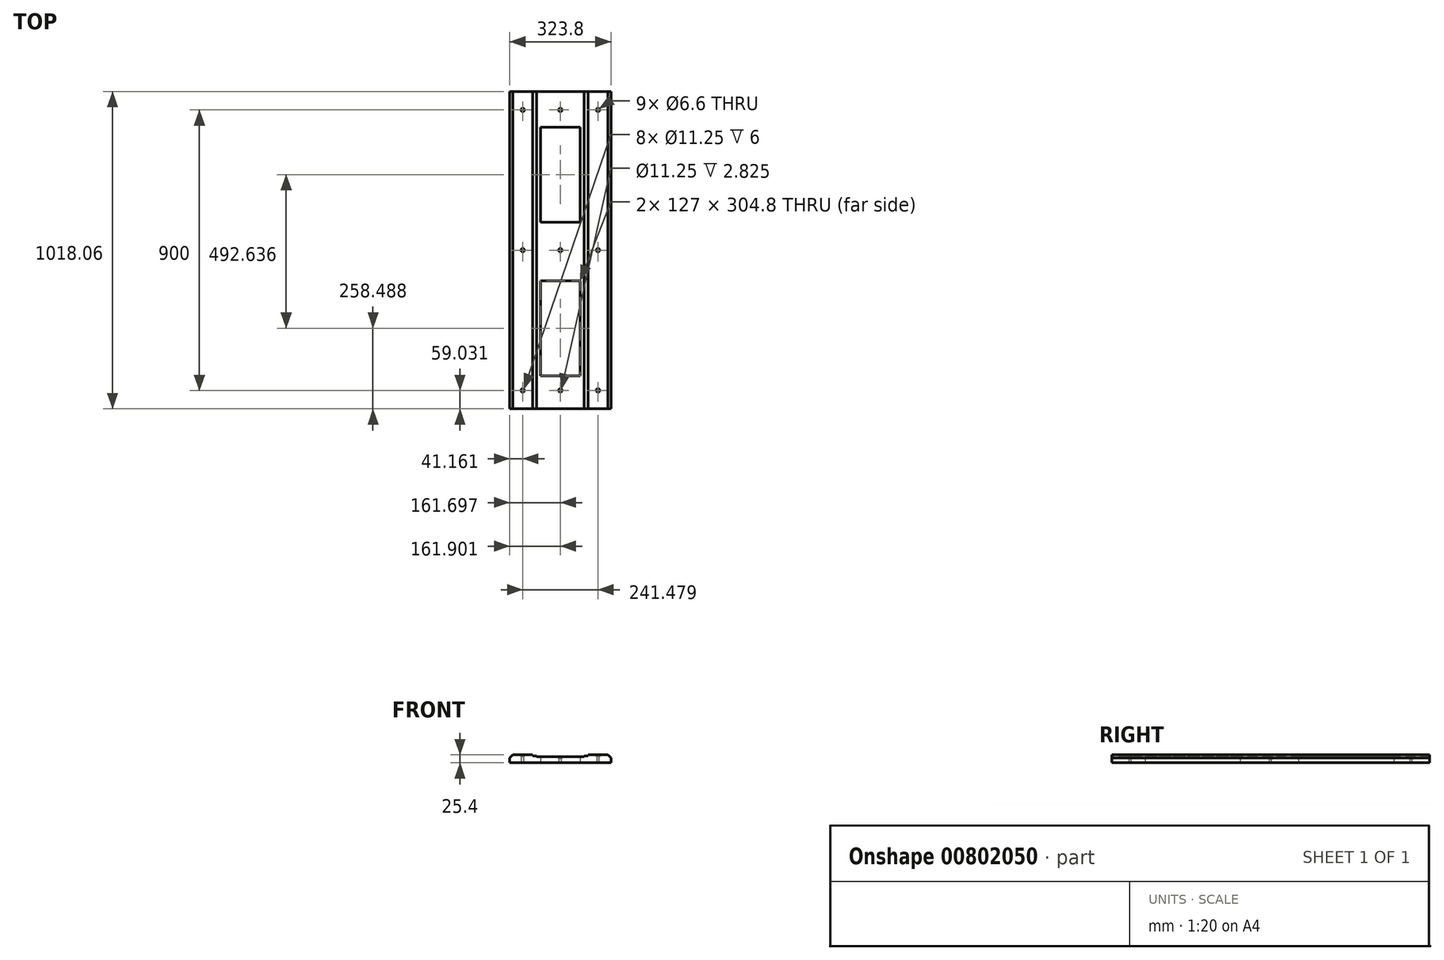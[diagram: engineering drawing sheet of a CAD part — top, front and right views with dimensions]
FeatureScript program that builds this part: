
annotation { "Feature Type Name" : "Feature", "Feature Type Description" : "" }
export const myFeature = defineFeature(function(context is Context, id is Id, definition is map)
    precondition{}
    {
        {
            var Q0;
            Q0=qCreatedBy(makeId("Top.planeOp"),FACE);
            var sketch = newSketch(context, id + "F0", { "sketchPlane" : qUnion([Q0])});
            skLineSegment(sketch, "E0.bottom", {"start": v(0, 0) * mm, "end": v(-323.8, 0) * mm});
            skLineSegment(sketch, "E0.top", {"start": v(0, 1018.06) * mm, "end": v(-323.8, 1018.06) * mm});
            skLineSegment(sketch, "E0.left", {"start": v(0, 0) * mm, "end": v(0, 1018.06) * mm});
            skLineSegment(sketch, "E0.right", {"start": v(-323.8, 0) * mm, "end": v(-323.8, 1018.06) * mm});
            skLineSegment(sketch, "E1.bottom", {"start": v(-225.6, 903.52) * mm, "end": v(-98.6, 903.52) * mm});
            skLineSegment(sketch, "E1.top", {"start": v(-225.6, 598.72) * mm, "end": v(-98.6, 598.72) * mm});
            skLineSegment(sketch, "E1.left", {"start": v(-225.6, 903.52) * mm, "end": v(-225.6, 598.72) * mm});
            skLineSegment(sketch, "E1.right", {"start": v(-98.6, 903.52) * mm, "end": v(-98.6, 598.72) * mm});
            skLineSegment(sketch, "E2.bottom", {"start": v(-225.6, 410.89) * mm, "end": v(-98.6, 410.89) * mm});
            skLineSegment(sketch, "E2.top", {"start": v(-225.6, 106.09) * mm, "end": v(-98.6, 106.09) * mm});
            skLineSegment(sketch, "E2.left", {"start": v(-225.6, 410.89) * mm, "end": v(-225.6, 106.09) * mm});
            skLineSegment(sketch, "E2.right", {"start": v(-98.6, 410.89) * mm, "end": v(-98.6, 106.09) * mm});
            skSolve(sketch);
        }
        {
            var Q0;
            Q0=qSketchRegion(id+"F0",true);
            extrude(context, id + "F1", {"entities" : qUnion([Q0]), "depth" : 25.4 * mm});
        }
        {
            var Q0;
            Q0=makeQuery(id+"F1.opExtrude","CAP_FACE",FACE,{"disambiguationData":[OSD([sQuery(id+"F0.wireOp",EDGE,"E0.bottom"),sQuery(id+"F0.wireOp",EDGE,"E0.top"),sQuery(id+"F0.wireOp",EDGE,"E0.left"),sQuery(id+"F0.wireOp",EDGE,"E0.right"),sQuery(id+"F0.wireOp",EDGE,"E1.bottom"),sQuery(id+"F0.wireOp",EDGE,"E1.top"),sQuery(id+"F0.wireOp",EDGE,"E1.left"),sQuery(id+"F0.wireOp",EDGE,"E1.right"),sQuery(id+"F0.wireOp",EDGE,"E2.bottom"),sQuery(id+"F0.wireOp",EDGE,"E2.top"),sQuery(id+"F0.wireOp",EDGE,"E2.left"),sQuery(id+"F0.wireOp",EDGE,"E2.right")])],"isStart":false});
            var sketch = newSketch(context, id + "F2", { "sketchPlane" : qUnion([Q0])});
            skLineSegment(sketch, "E3.bottom", {"start": v(-73.2, 1034.07) * mm, "end": v(-251, 1034.07) * mm});
            skLineSegment(sketch, "E3.top", {"start": v(-73.2, -43.77) * mm, "end": v(-251, -43.77) * mm});
            skLineSegment(sketch, "E3.left", {"start": v(-73.2, 1034.07) * mm, "end": v(-73.2, -43.77) * mm});
            skLineSegment(sketch, "E3.right", {"start": v(-251, 1034.07) * mm, "end": v(-251, -43.77) * mm});
            skSolve(sketch);
        }
        {
            var Q0;
            Q0=qSketchRegion(id+"F2",true);
            extrude(context, id + "F3", {"entities" : qUnion([Q0]), "operationType" : NewBodyOperationType.REMOVE, "oppositeDirection" : true, "depth" : 3.17 * mm});
        }
        {
            var Q0;
            Q0=makeQuery(id+"F3.boolean.opBoolean","COPY",FACE,{"derivedFrom":makeQuery(id+"F3.opExtrude","CAP_FACE",FACE,{"disambiguationData":[OSD([sQuery(id+"F2.wireOp",EDGE,"E3.bottom"),sQuery(id+"F2.wireOp",EDGE,"E3.top"),sQuery(id+"F2.wireOp",EDGE,"E3.left"),sQuery(id+"F2.wireOp",EDGE,"E3.right")])],"isStart":false})});
            var sketch = newSketch(context, id + "F4", { "sketchPlane" : qUnion([Q0])});
            skLineSegment(sketch, "E4.bottom", {"start": v(-85.9, 1051.67) * mm, "end": v(-238.3, 1051.67) * mm});
            skLineSegment(sketch, "E4.top", {"start": v(-85.9, -42.85) * mm, "end": v(-238.3, -42.85) * mm});
            skLineSegment(sketch, "E4.left", {"start": v(-85.9, 1051.67) * mm, "end": v(-85.9, -42.85) * mm});
            skLineSegment(sketch, "E4.right", {"start": v(-238.3, 1051.67) * mm, "end": v(-238.3, -42.85) * mm});
            skSolve(sketch);
        }
        {
            var Q0;
            Q0=qSketchRegion(id+"F4",true);
            extrude(context, id + "F5", {"entities" : qUnion([Q0]), "operationType" : NewBodyOperationType.REMOVE, "oppositeDirection" : true, "depth" : 3.17 * mm});
        }
        {
            var Q0;
            Q0=makeQuery(id+"F1.opExtrude","CAP_EDGE",EDGE,{"disambiguationData":[OSD([sQuery(id+"F0.wireOp",EDGE,"E0.right")])],"isStart":false});
            var Q1;
            Q1=makeQuery(id+"F1.opExtrude","CAP_EDGE",EDGE,{"disambiguationData":[OSD([sQuery(id+"F0.wireOp",EDGE,"E0.left")])],"isStart":false});
            chamfer(context, id + "F6", {"entities" : qUnion([Q0, Q1]), "width" : 9.52 * mm, "tangentPropagation" : true});
        }
        {
            var Q0;
            {var subQ0=sQuery(id+"F0.wireOp",EDGE,"E0.bottom");var subQ1=sQuery(id+"F0.wireOp",EDGE,"E0.top");var subQ2=sQuery(id+"F0.wireOp",EDGE,"E0.left");Q0=makeQuery(id+"F3.boolean.opBoolean","SPLIT",FACE,{"disambiguationData":[TD([makeQuery(id+"F1.opExtrude","SWEPT_FACE",FACE,{"disambiguationData":[OSD([subQ2])]})])],"derivedFrom":makeQuery(id+"F1.opExtrude","CAP_FACE",FACE,{"disambiguationData":[OSD([subQ0,subQ1,subQ2,sQuery(id+"F0.wireOp",EDGE,"E0.right"),sQuery(id+"F0.wireOp",EDGE,"E1.bottom"),sQuery(id+"F0.wireOp",EDGE,"E1.top"),sQuery(id+"F0.wireOp",EDGE,"E1.left"),sQuery(id+"F0.wireOp",EDGE,"E1.right"),sQuery(id+"F0.wireOp",EDGE,"E2.bottom"),sQuery(id+"F0.wireOp",EDGE,"E2.top"),sQuery(id+"F0.wireOp",EDGE,"E2.left"),sQuery(id+"F0.wireOp",EDGE,"E2.right")])],"isStart":false})});}
            var sketch = newSketch(context, id + "F7", { "sketchPlane" : qUnion([Q0])});
            skLineSegment(sketch, "E5", {"start": v(-41.16, 0) * mm, "end": v(-41.16, 1018.06) * mm, "construction": true});
            skPoint(sketch, "E6", {"position": v(-41.16, 509.03) * mm});
            skPoint(sketch, "E7.0.3.0", {"position": v(-41.16, 959.03) * mm});
            skLineSegment(sketch, "E7.direction1", {"start": v(-41.16, 509.03) * mm, "end": v(-16.36, 509.03) * mm, "construction": true});
            skLineSegment(sketch, "E7.direction2", {"start": v(-41.16, 509.03) * mm, "end": v(-41.16, 659.03) * mm, "construction": true});
            skPoint(sketch, "E8.0.3.0", {"position": v(-41.16, 59.03) * mm});
            skLineSegment(sketch, "E8.direction1", {"start": v(-41.16, 509.03) * mm, "end": v(-16.16, 509.03) * mm, "construction": true});
            skLineSegment(sketch, "E8.direction2", {"start": v(-41.16, 509.03) * mm, "end": v(-41.16, 359.03) * mm, "construction": true});
            skSolve(sketch);
        }
        {
            var Q0;
            Q0=sQuery(id+"F7.wireOp",VERTEX,"E8.0.3.0");
            var Q1;
            Q1=sQuery(id+"F7.wireOp",VERTEX,"E8.0.2.0");
            var Q2;
            Q2=sQuery(id+"F7.wireOp",VERTEX,"E8.0.1.0");
            var Q3;
            Q3=sQuery(id+"F7.wireOp",VERTEX,"E6");
            var Q4;
            Q4=sQuery(id+"F7.wireOp",VERTEX,"E7.0.1.0");
            var Q5;
            Q5=sQuery(id+"F7.wireOp",VERTEX,"E7.0.2.0");
            var Q6;
            Q6=sQuery(id+"F7.wireOp",VERTEX,"E7.0.3.0");
            var Q7;
            Q7=makeQuery(id+"F1.opExtrude","SWEPT_BODY",BODY,{"disambiguationData":[OSD([sQuery(id+"F0.wireOp",EDGE,"E0.bottom"),sQuery(id+"F0.wireOp",EDGE,"E0.top"),sQuery(id+"F0.wireOp",EDGE,"E0.left"),sQuery(id+"F0.wireOp",EDGE,"E0.right"),sQuery(id+"F0.wireOp",EDGE,"E1.bottom"),sQuery(id+"F0.wireOp",EDGE,"E1.top"),sQuery(id+"F0.wireOp",EDGE,"E1.left"),sQuery(id+"F0.wireOp",EDGE,"E1.right"),sQuery(id+"F0.wireOp",EDGE,"E2.bottom"),sQuery(id+"F0.wireOp",EDGE,"E2.top"),sQuery(id+"F0.wireOp",EDGE,"E2.left"),sQuery(id+"F0.wireOp",EDGE,"E2.right")])]});
            hole(context, id + "F8", {"style" : HoleStyle.C_BORE, "endStyle" : HoleEndStyle.BLIND, "standardTappedOrClearance" : lookupTablePath({ "standard" : "ISO", "fit" : "Normal", "size" : "M6", "type" : "Clearance" }), "standardBlindInLast" : lookupTablePath({ "fit" : "Standard", "standard" : "ISO", "size" : "M6", "type" : "Clearance" }), "holeDiameter" : 6.6 * mm, "cBoreDiameter" : 11.25 * mm, "cBoreDepth" : 6 * mm, "holeDepth" : 25 * mm, "isTappedThrough" : true, "tappedDepth" : 10.25 * mm, "tapClearance" : 3, "startFromSketch" : true, "locations" : qUnion([Q0, Q1, Q2, Q3, Q4, Q5, Q6]), "scope" : qUnion([Q7])});
        }
        {
            var Q0;
            {var subQ0=sQuery(id+"F0.wireOp",EDGE,"E0.bottom");var subQ1=sQuery(id+"F0.wireOp",EDGE,"E0.right");var subQ2=sQuery(id+"F0.wireOp",EDGE,"E0.top");Q0=makeQuery(id+"F3.boolean.opBoolean","SPLIT",FACE,{"disambiguationData":[TD([makeQuery(id+"F1.opExtrude","SWEPT_FACE",FACE,{"disambiguationData":[OSD([subQ1])]})])],"derivedFrom":makeQuery(id+"F1.opExtrude","CAP_FACE",FACE,{"disambiguationData":[OSD([subQ0,subQ2,sQuery(id+"F0.wireOp",EDGE,"E0.left"),subQ1,sQuery(id+"F0.wireOp",EDGE,"E1.bottom"),sQuery(id+"F0.wireOp",EDGE,"E1.top"),sQuery(id+"F0.wireOp",EDGE,"E1.left"),sQuery(id+"F0.wireOp",EDGE,"E1.right"),sQuery(id+"F0.wireOp",EDGE,"E2.bottom"),sQuery(id+"F0.wireOp",EDGE,"E2.top"),sQuery(id+"F0.wireOp",EDGE,"E2.left"),sQuery(id+"F0.wireOp",EDGE,"E2.right")])],"isStart":false})});}
            var sketch = newSketch(context, id + "F9", { "sketchPlane" : qUnion([Q0])});
            skLineSegment(sketch, "E9", {"start": v(-282.64, 1018.06) * mm, "end": v(-282.64, 0) * mm, "construction": true});
            skPoint(sketch, "E10", {"position": v(-282.64, 509.03) * mm});
            skPoint(sketch, "E11.0.3.0", {"position": v(-282.64, 959.03) * mm});
            skLineSegment(sketch, "E11.direction1", {"start": v(-282.64, 509.03) * mm, "end": v(-257.64, 509.03) * mm, "construction": true});
            skLineSegment(sketch, "E11.direction2", {"start": v(-282.64, 509.03) * mm, "end": v(-282.64, 659.03) * mm, "construction": true});
            skPoint(sketch, "E12.0.3.0", {"position": v(-282.64, 59.03) * mm});
            skLineSegment(sketch, "E12.direction2", {"start": v(-282.64, 509.03) * mm, "end": v(-282.64, 359.03) * mm, "construction": true});
            skSolve(sketch);
        }
        {
            var Q0;
            Q0=sQuery(id+"F9.wireOp",VERTEX,"E12.0.3.0");
            var Q1;
            Q1=sQuery(id+"F9.wireOp",VERTEX,"E12.0.2.0");
            var Q2;
            Q2=sQuery(id+"F9.wireOp",VERTEX,"E12.0.1.0");
            var Q3;
            Q3=sQuery(id+"F9.wireOp",VERTEX,"E10");
            var Q4;
            Q4=sQuery(id+"F9.wireOp",VERTEX,"E11.0.1.0");
            var Q5;
            Q5=sQuery(id+"F9.wireOp",VERTEX,"E11.0.2.0");
            var Q6;
            Q6=sQuery(id+"F9.wireOp",VERTEX,"E11.0.3.0");
            var Q7;
            Q7=makeQuery(id+"F1.opExtrude","SWEPT_BODY",BODY,{"disambiguationData":[OSD([sQuery(id+"F0.wireOp",EDGE,"E0.bottom"),sQuery(id+"F0.wireOp",EDGE,"E0.top"),sQuery(id+"F0.wireOp",EDGE,"E0.left"),sQuery(id+"F0.wireOp",EDGE,"E0.right"),sQuery(id+"F0.wireOp",EDGE,"E1.bottom"),sQuery(id+"F0.wireOp",EDGE,"E1.top"),sQuery(id+"F0.wireOp",EDGE,"E1.left"),sQuery(id+"F0.wireOp",EDGE,"E1.right"),sQuery(id+"F0.wireOp",EDGE,"E2.bottom"),sQuery(id+"F0.wireOp",EDGE,"E2.top"),sQuery(id+"F0.wireOp",EDGE,"E2.left"),sQuery(id+"F0.wireOp",EDGE,"E2.right")])]});
            hole(context, id + "F10", {"style" : HoleStyle.C_BORE, "endStyle" : HoleEndStyle.BLIND, "standardTappedOrClearance" : lookupTablePath({ "standard" : "ISO", "fit" : "Normal", "size" : "M6", "type" : "Clearance" }), "standardBlindInLast" : lookupTablePath({ "fit" : "Standard", "standard" : "ISO", "size" : "M6", "type" : "Clearance" }), "holeDiameter" : 6.6 * mm, "cBoreDiameter" : 11.25 * mm, "cBoreDepth" : 6 * mm, "holeDepth" : 25 * mm, "isTappedThrough" : true, "tappedDepth" : 10.25 * mm, "tapClearance" : 3, "startFromSketch" : true, "locations" : qUnion([Q0, Q1, Q2, Q3, Q4, Q5, Q6]), "scope" : qUnion([Q7])});
        }
        {
            var Q0;
            Q0=makeQuery(id+"F3.boolean.opBoolean","COPY",FACE,{"derivedFrom":makeQuery(id+"F3.opExtrude","CAP_FACE",FACE,{"disambiguationData":[OSD([sQuery(id+"F2.wireOp",EDGE,"E3.bottom"),sQuery(id+"F2.wireOp",EDGE,"E3.top"),sQuery(id+"F2.wireOp",EDGE,"E3.left"),sQuery(id+"F2.wireOp",EDGE,"E3.right")])],"isStart":false})});
            var sketch = newSketch(context, id + "F11", { "sketchPlane" : qUnion([Q0])});
            skLineSegment(sketch, "E13", {"start": v(-282.64, 59.03) * mm, "end": v(-41.16, 59.03) * mm, "construction": true});
            skCircle(sketch, "E14", {"center": v(-41.16, 59.03) * mm, "radius": 5.63 * mm, "construction": true});
            skCircle(sketch, "E15", {"center": v(-282.64, 59.03) * mm, "radius": 5.63 * mm});
            skPoint(sketch, "E16", {"position": v(-161.9, 59.03) * mm});
            skSolve(sketch);
        }
        {
            var Q0;
            Q0=makeQuery(id+"F5.boolean.opBoolean","COPY",FACE,{"derivedFrom":makeQuery(id+"F5.opExtrude","CAP_FACE",FACE,{"disambiguationData":[OSD([sQuery(id+"F4.wireOp",EDGE,"E4.bottom"),sQuery(id+"F4.wireOp",EDGE,"E4.top"),sQuery(id+"F4.wireOp",EDGE,"E4.left"),sQuery(id+"F4.wireOp",EDGE,"E4.right")])],"isStart":false})});
            var sketch = newSketch(context, id + "F12", { "sketchPlane" : qUnion([Q0])});
            skCircle(sketch, "E17", {"center": v(-282.64, 959.03) * mm, "radius": 5.62 * mm, "construction": true});
            skCircle(sketch, "E18", {"center": v(-41.16, 959.03) * mm, "radius": 5.62 * mm, "construction": true});
            skLineSegment(sketch, "E19", {"start": v(-282.64, 959.03) * mm, "end": v(-41.16, 959.03) * mm, "construction": true});
            skPoint(sketch, "E20", {"position": v(-161.9, 959.03) * mm});
            skCircle(sketch, "E21", {"center": v(-282.64, 509.03) * mm, "radius": 5.62 * mm, "construction": true});
            skCircle(sketch, "E22", {"center": v(-41.16, 509.03) * mm, "radius": 5.62 * mm, "construction": true});
            skLineSegment(sketch, "E23", {"start": v(-282.64, 509.03) * mm, "end": v(-41.16, 509.03) * mm, "construction": true});
            skPoint(sketch, "E24", {"position": v(-161.9, 509.03) * mm});
            skSolve(sketch);
        }
        {
            var Q0;
            Q0=sQuery(id+"F11.wireOp",VERTEX,"E16");
            var Q1;
            Q1=sQuery(id+"F12.wireOp",VERTEX,"E24");
            var Q2;
            Q2=sQuery(id+"F12.wireOp",VERTEX,"E20");
            var Q3;
            Q3=makeQuery(id+"F1.opExtrude","SWEPT_BODY",BODY,{"disambiguationData":[OSD([sQuery(id+"F0.wireOp",EDGE,"E0.bottom"),sQuery(id+"F0.wireOp",EDGE,"E0.top"),sQuery(id+"F0.wireOp",EDGE,"E0.left"),sQuery(id+"F0.wireOp",EDGE,"E0.right"),sQuery(id+"F0.wireOp",EDGE,"E1.bottom"),sQuery(id+"F0.wireOp",EDGE,"E1.top"),sQuery(id+"F0.wireOp",EDGE,"E1.left"),sQuery(id+"F0.wireOp",EDGE,"E1.right"),sQuery(id+"F0.wireOp",EDGE,"E2.bottom"),sQuery(id+"F0.wireOp",EDGE,"E2.top"),sQuery(id+"F0.wireOp",EDGE,"E2.left"),sQuery(id+"F0.wireOp",EDGE,"E2.right")])]});
            hole(context, id + "F13", {"style" : HoleStyle.C_BORE, "endStyle" : HoleEndStyle.THROUGH, "standardTappedOrClearance" : lookupTablePath({ "standard" : "ISO", "fit" : "Normal", "size" : "M6", "type" : "Clearance" }), "standardBlindInLast" : lookupTablePath({ "fit" : "Standard", "standard" : "ISO", "size" : "M6", "type" : "Clearance" }), "holeDiameter" : 6.6 * mm, "cBoreDiameter" : 11.25 * mm, "cBoreDepth" : 6 * mm, "isTappedThrough" : true, "tappedDepth" : 10.25 * mm, "tapClearance" : 3, "startFromSketch" : true, "locations" : qUnion([Q0, Q1, Q2]), "scope" : qUnion([Q3])});
        }
    });
